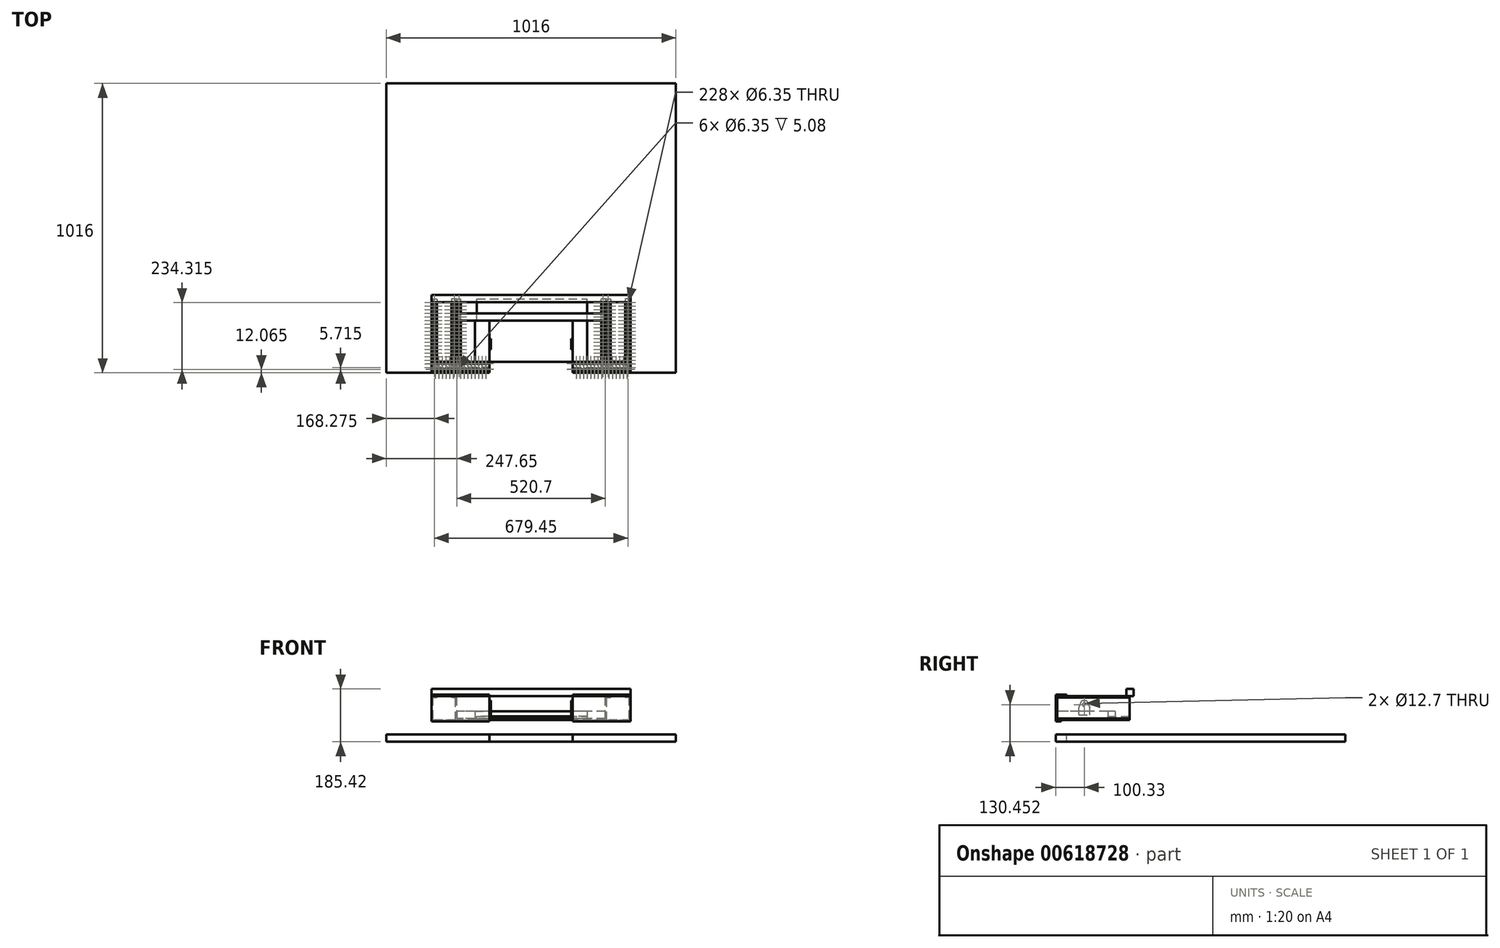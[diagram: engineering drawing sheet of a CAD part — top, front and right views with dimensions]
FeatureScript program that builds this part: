
annotation { "Feature Type Name" : "Feature", "Feature Type Description" : "" }
export const myFeature = defineFeature(function(context is Context, id is Id, definition is map)
    precondition{}
    {
        {
            var Q0;
            Q0=qCreatedBy(makeId("Top.planeOp"),FACE);
            var sketch = newSketch(context, id + "F0", { "sketchPlane" : qUnion([Q0])});
            skLineSegment(sketch, "E0.bottom", {"start": v(508, 508) * mm, "end": v(-508, 508) * mm});
            skLineSegment(sketch, "E0.top", {"start": v(508, -508) * mm, "end": v(-508, -508) * mm});
            skLineSegment(sketch, "E0.left", {"start": v(508, 508) * mm, "end": v(508, -508) * mm});
            skLineSegment(sketch, "E0.right", {"start": v(-508, 508) * mm, "end": v(-508, -508) * mm});
            skPoint(sketch, "E0.middle", {"position": v(0, 0) * mm});
            skSolve(sketch);
        }
        {
            var Q0;
            Q0=qSketchRegion(id+"F0",true);
            extrude(context, id + "F1", {"entities" : qUnion([Q0]), "depth" : 25.4 * mm, "offsetDistance" : 25.4 * mm});
        }
        {
            var Q0;
            Q0=makeQuery(id+"F1.opExtrude","SWEPT_FACE",FACE,{"disambiguationData":[OSD([sQuery(id+"F0.wireOp",EDGE,"E0.top")])]});
            var sketch = newSketch(context, id + "F2", { "sketchPlane" : qUnion([Q0])});
            skLineSegment(sketch, "E1.bottom", {"start": v(-349.25, 165.1) * mm, "end": v(349.25, 165.1) * mm});
            skLineSegment(sketch, "E1.top", {"start": v(-349.25, 76.2) * mm, "end": v(349.25, 76.2) * mm});
            skLineSegment(sketch, "E1.left", {"start": v(-349.25, 165.1) * mm, "end": v(-349.25, 76.2) * mm});
            skLineSegment(sketch, "E1.right", {"start": v(349.25, 165.1) * mm, "end": v(349.25, 76.2) * mm});
            skSolve(sketch);
        }
        {
            var Q0;
            Q0=qSketchRegion(id+"F2",true);
            extrude(context, id + "F3", {"entities" : qUnion([Q0]), "oppositeDirection" : true, "depth" : 5.08 * mm, "offsetDistance" : 25.4 * mm});
        }
        {
            var Q0;
            Q0=makeQuery(id+"F3.opExtrude","SWEPT_FACE",FACE,{"disambiguationData":[OSD([sQuery(id+"F2.wireOp",EDGE,"E1.bottom")])]});
            var sketch = newSketch(context, id + "F4", { "sketchPlane" : qUnion([Q0])});
            skLineSegment(sketch, "E2.bottom", {"start": v(-349.25, -469.9) * mm, "end": v(349.25, -469.9) * mm});
            skLineSegment(sketch, "E2.top", {"start": v(-349.25, -508) * mm, "end": v(349.25, -508) * mm});
            skLineSegment(sketch, "E2.left", {"start": v(-349.25, -469.9) * mm, "end": v(-349.25, -508) * mm});
            skLineSegment(sketch, "E2.right", {"start": v(349.25, -469.9) * mm, "end": v(349.25, -508) * mm});
            skCircle(sketch, "E3", {"center": v(-336.55, -476.25) * mm, "radius": 3.18 * mm});
            skCircle(sketch, "E4.0.1.0", {"center": v(-335.43, -495.27) * mm, "radius": 3.18 * mm});
            skCircle(sketch, "E4.1.0.0", {"center": v(-323.85, -476.25) * mm, "radius": 3.18 * mm});
            skCircle(sketch, "E4.1.1.0", {"center": v(-322.73, -495.27) * mm, "radius": 3.18 * mm});
            skCircle(sketch, "E4.2.0.0", {"center": v(-311.15, -476.25) * mm, "radius": 3.18 * mm});
            skCircle(sketch, "E4.2.1.0", {"center": v(-310.03, -495.27) * mm, "radius": 3.18 * mm});
            skCircle(sketch, "E4.3.0.0", {"center": v(-298.45, -476.25) * mm, "radius": 3.18 * mm});
            skCircle(sketch, "E4.3.1.0", {"center": v(-297.33, -495.27) * mm, "radius": 3.18 * mm});
            skCircle(sketch, "E4.4.0.0", {"center": v(-285.75, -476.25) * mm, "radius": 3.18 * mm});
            skCircle(sketch, "E4.4.1.0", {"center": v(-284.63, -495.27) * mm, "radius": 3.18 * mm});
            skCircle(sketch, "E4.5.0.0", {"center": v(-273.05, -476.25) * mm, "radius": 3.18 * mm});
            skCircle(sketch, "E4.5.1.0", {"center": v(-271.93, -495.27) * mm, "radius": 3.18 * mm});
            skCircle(sketch, "E4.6.0.0", {"center": v(-260.35, -476.25) * mm, "radius": 3.18 * mm});
            skCircle(sketch, "E4.6.1.0", {"center": v(-259.23, -495.27) * mm, "radius": 3.18 * mm});
            skCircle(sketch, "E4.7.0.0", {"center": v(-247.65, -476.25) * mm, "radius": 3.18 * mm});
            skCircle(sketch, "E4.7.1.0", {"center": v(-246.53, -495.27) * mm, "radius": 3.18 * mm});
            skCircle(sketch, "E4.8.0.0", {"center": v(-234.95, -476.25) * mm, "radius": 3.18 * mm});
            skCircle(sketch, "E4.8.1.0", {"center": v(-233.83, -495.27) * mm, "radius": 3.18 * mm});
            skCircle(sketch, "E4.9.0.0", {"center": v(-222.25, -476.25) * mm, "radius": 3.18 * mm});
            skCircle(sketch, "E4.9.1.0", {"center": v(-221.13, -495.27) * mm, "radius": 3.18 * mm});
            skCircle(sketch, "E4.10.0.0", {"center": v(-209.55, -476.25) * mm, "radius": 3.18 * mm});
            skCircle(sketch, "E4.10.1.0", {"center": v(-208.43, -495.27) * mm, "radius": 3.18 * mm});
            skCircle(sketch, "E4.11.0.0", {"center": v(-196.85, -476.25) * mm, "radius": 3.18 * mm});
            skCircle(sketch, "E4.11.1.0", {"center": v(-195.73, -495.27) * mm, "radius": 3.18 * mm});
            skCircle(sketch, "E4.12.0.0", {"center": v(-184.15, -476.25) * mm, "radius": 3.18 * mm});
            skCircle(sketch, "E4.12.1.0", {"center": v(-183.03, -495.27) * mm, "radius": 3.18 * mm});
            skCircle(sketch, "E4.13.0.0", {"center": v(-171.45, -476.25) * mm, "radius": 3.18 * mm});
            skCircle(sketch, "E4.13.1.0", {"center": v(-170.33, -495.27) * mm, "radius": 3.18 * mm});
            skCircle(sketch, "E4.14.0.0", {"center": v(-158.75, -476.25) * mm, "radius": 3.18 * mm});
            skCircle(sketch, "E4.14.1.0", {"center": v(-157.63, -495.27) * mm, "radius": 3.18 * mm});
            skCircle(sketch, "E4.15.0.0", {"center": v(-146.05, -476.25) * mm, "radius": 3.18 * mm});
            skCircle(sketch, "E4.15.1.0", {"center": v(-144.93, -495.27) * mm, "radius": 3.18 * mm});
            skCircle(sketch, "E4.16.0.0", {"center": v(-133.35, -476.25) * mm, "radius": 3.18 * mm});
            skCircle(sketch, "E4.16.1.0", {"center": v(-132.23, -495.27) * mm, "radius": 3.18 * mm});
            skCircle(sketch, "E4.17.0.0", {"center": v(-120.65, -476.25) * mm, "radius": 3.18 * mm});
            skCircle(sketch, "E4.17.1.0", {"center": v(-119.53, -495.27) * mm, "radius": 3.18 * mm});
            skCircle(sketch, "E4.18.0.0", {"center": v(-107.95, -476.25) * mm, "radius": 3.18 * mm});
            skCircle(sketch, "E4.18.1.0", {"center": v(-106.83, -495.27) * mm, "radius": 3.18 * mm});
            skCircle(sketch, "E4.19.0.0", {"center": v(-95.25, -476.25) * mm, "radius": 3.18 * mm});
            skCircle(sketch, "E4.19.1.0", {"center": v(-94.13, -495.27) * mm, "radius": 3.18 * mm});
            skCircle(sketch, "E4.20.0.0", {"center": v(-82.55, -476.25) * mm, "radius": 3.18 * mm});
            skCircle(sketch, "E4.20.1.0", {"center": v(-81.43, -495.27) * mm, "radius": 3.18 * mm});
            skCircle(sketch, "E4.21.0.0", {"center": v(-69.85, -476.25) * mm, "radius": 3.18 * mm});
            skCircle(sketch, "E4.21.1.0", {"center": v(-68.73, -495.27) * mm, "radius": 3.18 * mm});
            skCircle(sketch, "E4.22.0.0", {"center": v(-57.15, -476.25) * mm, "radius": 3.18 * mm});
            skCircle(sketch, "E4.22.1.0", {"center": v(-56.03, -495.27) * mm, "radius": 3.18 * mm});
            skCircle(sketch, "E4.23.0.0", {"center": v(-44.45, -476.25) * mm, "radius": 3.18 * mm});
            skCircle(sketch, "E4.23.1.0", {"center": v(-43.33, -495.27) * mm, "radius": 3.18 * mm});
            skCircle(sketch, "E4.24.0.0", {"center": v(-31.75, -476.25) * mm, "radius": 3.18 * mm});
            skCircle(sketch, "E4.24.1.0", {"center": v(-30.63, -495.27) * mm, "radius": 3.18 * mm});
            skCircle(sketch, "E4.25.0.0", {"center": v(-19.05, -476.25) * mm, "radius": 3.18 * mm});
            skCircle(sketch, "E4.25.1.0", {"center": v(-17.93, -495.27) * mm, "radius": 3.18 * mm});
            skCircle(sketch, "E4.26.0.0", {"center": v(-6.35, -476.25) * mm, "radius": 3.18 * mm});
            skCircle(sketch, "E4.26.1.0", {"center": v(-5.23, -495.27) * mm, "radius": 3.18 * mm});
            skCircle(sketch, "E4.27.0.0", {"center": v(6.35, -476.25) * mm, "radius": 3.18 * mm});
            skCircle(sketch, "E4.27.1.0", {"center": v(7.47, -495.27) * mm, "radius": 3.18 * mm});
            skCircle(sketch, "E4.28.0.0", {"center": v(19.05, -476.25) * mm, "radius": 3.18 * mm});
            skCircle(sketch, "E4.28.1.0", {"center": v(20.17, -495.27) * mm, "radius": 3.18 * mm});
            skCircle(sketch, "E4.29.0.0", {"center": v(31.75, -476.25) * mm, "radius": 3.18 * mm});
            skCircle(sketch, "E4.29.1.0", {"center": v(32.87, -495.27) * mm, "radius": 3.18 * mm});
            skCircle(sketch, "E4.30.0.0", {"center": v(44.45, -476.25) * mm, "radius": 3.18 * mm});
            skCircle(sketch, "E4.30.1.0", {"center": v(45.57, -495.27) * mm, "radius": 3.18 * mm});
            skCircle(sketch, "E4.31.0.0", {"center": v(57.15, -476.25) * mm, "radius": 3.18 * mm});
            skCircle(sketch, "E4.31.1.0", {"center": v(58.27, -495.27) * mm, "radius": 3.18 * mm});
            skCircle(sketch, "E4.32.0.0", {"center": v(69.85, -476.25) * mm, "radius": 3.18 * mm});
            skCircle(sketch, "E4.32.1.0", {"center": v(70.97, -495.27) * mm, "radius": 3.18 * mm});
            skCircle(sketch, "E4.33.0.0", {"center": v(82.55, -476.25) * mm, "radius": 3.18 * mm});
            skCircle(sketch, "E4.33.1.0", {"center": v(83.67, -495.27) * mm, "radius": 3.18 * mm});
            skCircle(sketch, "E4.34.0.0", {"center": v(95.25, -476.25) * mm, "radius": 3.18 * mm});
            skCircle(sketch, "E4.34.1.0", {"center": v(96.37, -495.27) * mm, "radius": 3.18 * mm});
            skCircle(sketch, "E4.35.0.0", {"center": v(107.95, -476.25) * mm, "radius": 3.18 * mm});
            skCircle(sketch, "E4.35.1.0", {"center": v(109.07, -495.27) * mm, "radius": 3.18 * mm});
            skCircle(sketch, "E4.36.0.0", {"center": v(120.65, -476.25) * mm, "radius": 3.18 * mm});
            skCircle(sketch, "E4.36.1.0", {"center": v(121.77, -495.27) * mm, "radius": 3.18 * mm});
            skCircle(sketch, "E4.37.0.0", {"center": v(133.35, -476.25) * mm, "radius": 3.18 * mm});
            skCircle(sketch, "E4.37.1.0", {"center": v(134.47, -495.27) * mm, "radius": 3.18 * mm});
            skCircle(sketch, "E4.38.0.0", {"center": v(146.05, -476.25) * mm, "radius": 3.18 * mm});
            skCircle(sketch, "E4.38.1.0", {"center": v(147.17, -495.27) * mm, "radius": 3.18 * mm});
            skCircle(sketch, "E4.39.0.0", {"center": v(158.75, -476.25) * mm, "radius": 3.18 * mm});
            skCircle(sketch, "E4.39.1.0", {"center": v(159.87, -495.27) * mm, "radius": 3.18 * mm});
            skCircle(sketch, "E4.40.0.0", {"center": v(171.45, -476.25) * mm, "radius": 3.18 * mm});
            skCircle(sketch, "E4.40.1.0", {"center": v(172.57, -495.27) * mm, "radius": 3.18 * mm});
            skCircle(sketch, "E4.41.0.0", {"center": v(184.15, -476.25) * mm, "radius": 3.18 * mm});
            skCircle(sketch, "E4.41.1.0", {"center": v(185.27, -495.27) * mm, "radius": 3.18 * mm});
            skCircle(sketch, "E4.42.0.0", {"center": v(196.85, -476.25) * mm, "radius": 3.18 * mm});
            skCircle(sketch, "E4.42.1.0", {"center": v(197.97, -495.27) * mm, "radius": 3.18 * mm});
            skCircle(sketch, "E4.43.0.0", {"center": v(209.55, -476.25) * mm, "radius": 3.18 * mm});
            skCircle(sketch, "E4.43.1.0", {"center": v(210.67, -495.27) * mm, "radius": 3.18 * mm});
            skCircle(sketch, "E4.44.0.0", {"center": v(222.25, -476.25) * mm, "radius": 3.18 * mm});
            skCircle(sketch, "E4.44.1.0", {"center": v(223.37, -495.27) * mm, "radius": 3.18 * mm});
            skCircle(sketch, "E4.45.0.0", {"center": v(234.95, -476.25) * mm, "radius": 3.18 * mm});
            skCircle(sketch, "E4.45.1.0", {"center": v(236.07, -495.27) * mm, "radius": 3.18 * mm});
            skCircle(sketch, "E4.46.0.0", {"center": v(247.65, -476.25) * mm, "radius": 3.18 * mm});
            skCircle(sketch, "E4.46.1.0", {"center": v(248.77, -495.27) * mm, "radius": 3.18 * mm});
            skCircle(sketch, "E4.47.0.0", {"center": v(260.35, -476.25) * mm, "radius": 3.18 * mm});
            skCircle(sketch, "E4.47.1.0", {"center": v(261.47, -495.27) * mm, "radius": 3.18 * mm});
            skCircle(sketch, "E4.48.0.0", {"center": v(273.05, -476.25) * mm, "radius": 3.18 * mm});
            skCircle(sketch, "E4.48.1.0", {"center": v(274.17, -495.27) * mm, "radius": 3.18 * mm});
            skCircle(sketch, "E4.49.0.0", {"center": v(285.75, -476.25) * mm, "radius": 3.18 * mm});
            skCircle(sketch, "E4.49.1.0", {"center": v(286.87, -495.27) * mm, "radius": 3.18 * mm});
            skCircle(sketch, "E4.50.0.0", {"center": v(298.45, -476.25) * mm, "radius": 3.18 * mm});
            skCircle(sketch, "E4.50.1.0", {"center": v(299.57, -495.27) * mm, "radius": 3.18 * mm});
            skCircle(sketch, "E4.51.0.0", {"center": v(311.15, -476.25) * mm, "radius": 3.18 * mm});
            skCircle(sketch, "E4.51.1.0", {"center": v(312.27, -495.27) * mm, "radius": 3.18 * mm});
            skCircle(sketch, "E4.52.0.0", {"center": v(323.85, -476.25) * mm, "radius": 3.18 * mm});
            skCircle(sketch, "E4.52.1.0", {"center": v(324.97, -495.27) * mm, "radius": 3.18 * mm});
            skCircle(sketch, "E4.53.0.0", {"center": v(336.55, -476.25) * mm, "radius": 3.18 * mm});
            skCircle(sketch, "E4.53.1.0", {"center": v(337.67, -495.27) * mm, "radius": 3.18 * mm});
            skLineSegment(sketch, "E4.direction1", {"start": v(-336.55, -476.25) * mm, "end": v(-323.85, -476.25) * mm, "construction": true});
            skLineSegment(sketch, "E4.direction2", {"start": v(-336.55, -476.25) * mm, "end": v(-335.43, -495.27) * mm, "construction": true});
            skSolve(sketch);
        }
        {
            var Q0;
            Q0=qSketchRegion(id+"F4",true);
            extrude(context, id + "F5", {"entities" : qUnion([Q0]), "oppositeDirection" : true, "depth" : 5.08 * mm, "offsetDistance" : 25.4 * mm});
        }
        {
            var Q0;
            Q0=makeQuery(id+"F3.opExtrude","SWEPT_FACE",FACE,{"disambiguationData":[OSD([sQuery(id+"F2.wireOp",EDGE,"E1.top")])]});
            var sketch = newSketch(context, id + "F6", { "sketchPlane" : qUnion([Q0])});
            skLineSegment(sketch, "E5.bottom", {"start": v(-349.25, 508) * mm, "end": v(349.25, 508) * mm});
            skLineSegment(sketch, "E5.top", {"start": v(-349.25, 488.95) * mm, "end": v(349.25, 488.95) * mm});
            skLineSegment(sketch, "E5.left", {"start": v(-349.25, 508) * mm, "end": v(-349.25, 488.95) * mm});
            skLineSegment(sketch, "E5.right", {"start": v(349.25, 508) * mm, "end": v(349.25, 488.95) * mm});
            skCircle(sketch, "E6", {"center": v(-336.55, 495.94) * mm, "radius": 3.18 * mm});
            skCircle(sketch, "E7.1.0.0", {"center": v(-323.85, 495.94) * mm, "radius": 3.18 * mm});
            skCircle(sketch, "E7.2.0.0", {"center": v(-311.15, 495.94) * mm, "radius": 3.18 * mm});
            skCircle(sketch, "E7.3.0.0", {"center": v(-298.45, 495.94) * mm, "radius": 3.18 * mm});
            skCircle(sketch, "E7.4.0.0", {"center": v(-285.75, 495.94) * mm, "radius": 3.18 * mm});
            skCircle(sketch, "E7.5.0.0", {"center": v(-273.05, 495.94) * mm, "radius": 3.18 * mm});
            skCircle(sketch, "E7.6.0.0", {"center": v(-260.35, 495.94) * mm, "radius": 3.18 * mm});
            skCircle(sketch, "E7.7.0.0", {"center": v(-247.65, 495.94) * mm, "radius": 3.18 * mm});
            skCircle(sketch, "E7.8.0.0", {"center": v(-234.95, 495.94) * mm, "radius": 3.18 * mm});
            skCircle(sketch, "E7.9.0.0", {"center": v(-222.25, 495.94) * mm, "radius": 3.18 * mm});
            skCircle(sketch, "E7.10.0.0", {"center": v(-209.55, 495.94) * mm, "radius": 3.18 * mm});
            skCircle(sketch, "E7.11.0.0", {"center": v(-196.85, 495.94) * mm, "radius": 3.18 * mm});
            skCircle(sketch, "E7.12.0.0", {"center": v(-184.15, 495.94) * mm, "radius": 3.18 * mm});
            skCircle(sketch, "E7.13.0.0", {"center": v(-171.45, 495.94) * mm, "radius": 3.18 * mm});
            skCircle(sketch, "E7.14.0.0", {"center": v(-158.75, 495.94) * mm, "radius": 3.18 * mm});
            skCircle(sketch, "E7.15.0.0", {"center": v(-146.05, 495.94) * mm, "radius": 3.18 * mm});
            skCircle(sketch, "E7.16.0.0", {"center": v(-133.35, 495.94) * mm, "radius": 3.18 * mm});
            skCircle(sketch, "E7.17.0.0", {"center": v(-120.65, 495.94) * mm, "radius": 3.18 * mm});
            skCircle(sketch, "E7.18.0.0", {"center": v(-107.95, 495.94) * mm, "radius": 3.18 * mm});
            skCircle(sketch, "E7.19.0.0", {"center": v(-95.25, 495.94) * mm, "radius": 3.18 * mm});
            skCircle(sketch, "E7.20.0.0", {"center": v(-82.55, 495.94) * mm, "radius": 3.18 * mm});
            skCircle(sketch, "E7.21.0.0", {"center": v(-69.85, 495.94) * mm, "radius": 3.18 * mm});
            skCircle(sketch, "E7.22.0.0", {"center": v(-57.15, 495.94) * mm, "radius": 3.18 * mm});
            skCircle(sketch, "E7.23.0.0", {"center": v(-44.45, 495.94) * mm, "radius": 3.18 * mm});
            skCircle(sketch, "E7.24.0.0", {"center": v(-31.75, 495.94) * mm, "radius": 3.18 * mm});
            skCircle(sketch, "E7.25.0.0", {"center": v(-19.05, 495.94) * mm, "radius": 3.18 * mm});
            skCircle(sketch, "E7.26.0.0", {"center": v(-6.35, 495.94) * mm, "radius": 3.18 * mm});
            skCircle(sketch, "E7.27.0.0", {"center": v(6.35, 495.94) * mm, "radius": 3.18 * mm});
            skCircle(sketch, "E7.28.0.0", {"center": v(19.05, 495.94) * mm, "radius": 3.18 * mm});
            skCircle(sketch, "E7.29.0.0", {"center": v(31.75, 495.94) * mm, "radius": 3.18 * mm});
            skCircle(sketch, "E7.30.0.0", {"center": v(44.45, 495.94) * mm, "radius": 3.18 * mm});
            skCircle(sketch, "E7.31.0.0", {"center": v(57.15, 495.94) * mm, "radius": 3.18 * mm});
            skCircle(sketch, "E7.32.0.0", {"center": v(69.85, 495.94) * mm, "radius": 3.18 * mm});
            skCircle(sketch, "E7.33.0.0", {"center": v(82.55, 495.94) * mm, "radius": 3.18 * mm});
            skCircle(sketch, "E7.34.0.0", {"center": v(95.25, 495.94) * mm, "radius": 3.18 * mm});
            skCircle(sketch, "E7.35.0.0", {"center": v(107.95, 495.94) * mm, "radius": 3.18 * mm});
            skCircle(sketch, "E7.36.0.0", {"center": v(120.65, 495.94) * mm, "radius": 3.18 * mm});
            skCircle(sketch, "E7.37.0.0", {"center": v(133.35, 495.94) * mm, "radius": 3.18 * mm});
            skCircle(sketch, "E7.38.0.0", {"center": v(146.05, 495.94) * mm, "radius": 3.18 * mm});
            skCircle(sketch, "E7.39.0.0", {"center": v(158.75, 495.94) * mm, "radius": 3.18 * mm});
            skCircle(sketch, "E7.40.0.0", {"center": v(171.45, 495.94) * mm, "radius": 3.18 * mm});
            skCircle(sketch, "E7.41.0.0", {"center": v(184.15, 495.94) * mm, "radius": 3.18 * mm});
            skCircle(sketch, "E7.42.0.0", {"center": v(196.85, 495.94) * mm, "radius": 3.18 * mm});
            skCircle(sketch, "E7.43.0.0", {"center": v(209.55, 495.94) * mm, "radius": 3.18 * mm});
            skCircle(sketch, "E7.44.0.0", {"center": v(222.25, 495.94) * mm, "radius": 3.18 * mm});
            skCircle(sketch, "E7.45.0.0", {"center": v(234.95, 495.94) * mm, "radius": 3.18 * mm});
            skCircle(sketch, "E7.46.0.0", {"center": v(247.65, 495.94) * mm, "radius": 3.18 * mm});
            skCircle(sketch, "E7.47.0.0", {"center": v(260.35, 495.94) * mm, "radius": 3.18 * mm});
            skCircle(sketch, "E7.48.0.0", {"center": v(273.05, 495.94) * mm, "radius": 3.18 * mm});
            skCircle(sketch, "E7.49.0.0", {"center": v(285.75, 495.94) * mm, "radius": 3.18 * mm});
            skCircle(sketch, "E7.50.0.0", {"center": v(298.45, 495.94) * mm, "radius": 3.18 * mm});
            skCircle(sketch, "E7.51.0.0", {"center": v(311.15, 495.94) * mm, "radius": 3.18 * mm});
            skCircle(sketch, "E7.52.0.0", {"center": v(323.85, 495.94) * mm, "radius": 3.18 * mm});
            skCircle(sketch, "E7.53.0.0", {"center": v(336.55, 495.94) * mm, "radius": 3.18 * mm});
            skLineSegment(sketch, "E7.direction1", {"start": v(-336.55, 495.94) * mm, "end": v(-323.85, 495.94) * mm, "construction": true});
            skSolve(sketch);
        }
        {
            var Q0;
            Q0=qSketchRegion(id+"F6",true);
            extrude(context, id + "F7", {"entities" : qUnion([Q0]), "operationType" : NewBodyOperationType.ADD, "depth" : 5.08 * mm, "offsetDistance" : 25.4 * mm});
        }
        {
            var Q0;
            Q0=makeQuery(id+"F3.opExtrude","CAP_FACE",FACE,{"disambiguationData":[OSD([sQuery(id+"F2.wireOp",EDGE,"E1.bottom"),sQuery(id+"F2.wireOp",EDGE,"E1.top"),sQuery(id+"F2.wireOp",EDGE,"E1.left"),sQuery(id+"F2.wireOp",EDGE,"E1.right")])],"isStart":false});
            var sketch = newSketch(context, id + "F8", { "sketchPlane" : qUnion([Q0])});
            skLineSegment(sketch, "E8.top", {"start": v(-349.25, 154.94) * mm, "end": v(-344.17, 154.94) * mm});
            skLineSegment(sketch, "E8.left", {"start": v(-349.25, 81.28) * mm, "end": v(-349.25, 154.94) * mm});
            skLineSegment(sketch, "E8.right", {"start": v(-344.17, 81.28) * mm, "end": v(-344.17, 154.94) * mm});
            skLineSegment(sketch, "E9.top", {"start": v(-265.43, 154.94) * mm, "end": v(-260.35, 154.94) * mm});
            skLineSegment(sketch, "E9.left", {"start": v(-265.43, 81.28) * mm, "end": v(-265.43, 154.94) * mm});
            skLineSegment(sketch, "E9.right", {"start": v(-260.35, 81.28) * mm, "end": v(-260.35, 154.94) * mm});
            skLineSegment(sketch, "E10", {"start": v(-265.43, 81.28) * mm, "end": v(-260.35, 81.28) * mm});
            skLineSegment(sketch, "E11", {"start": v(-349.25, 81.28) * mm, "end": v(-344.17, 81.28) * mm});
            skSolve(sketch);
        }
        {
            var Q0;
            Q0=qSketchRegion(id+"F8",true);
            extrude(context, id + "F9", {"entities" : qUnion([Q0]), "operationType" : NewBodyOperationType.ADD, "depth" : 254 * mm, "offsetDistance" : 25.4 * mm});
        }
        {
            var Q0;
            Q0=makeQuery(id+"F9.opExtrude","SWEPT_FACE",FACE,{"disambiguationData":[OSD([sQuery(id+"F8.wireOp",EDGE,"E8.top")])]});
            var sketch = newSketch(context, id + "F10", { "sketchPlane" : qUnion([Q0])});
            skLineSegment(sketch, "E12.bottom", {"start": v(349.25, -248.92) * mm, "end": v(330.2, -248.92) * mm});
            skLineSegment(sketch, "E12.top", {"start": v(349.25, -502.92) * mm, "end": v(330.2, -502.92) * mm});
            skLineSegment(sketch, "E12.left", {"start": v(349.25, -248.92) * mm, "end": v(349.25, -502.92) * mm});
            skLineSegment(sketch, "E12.right", {"start": v(330.2, -248.92) * mm, "end": v(330.2, -502.92) * mm});
            skLineSegment(sketch, "E13.bottom", {"start": v(260.35, -248.92) * mm, "end": v(279.4, -248.92) * mm});
            skLineSegment(sketch, "E13.top", {"start": v(260.35, -502.92) * mm, "end": v(279.4, -502.92) * mm});
            skLineSegment(sketch, "E13.left", {"start": v(260.35, -248.92) * mm, "end": v(260.35, -502.92) * mm});
            skLineSegment(sketch, "E13.right", {"start": v(279.4, -248.92) * mm, "end": v(279.4, -502.92) * mm});
            skCircle(sketch, "E14", {"center": v(269.88, -261.62) * mm, "radius": 3.18 * mm});
            skCircle(sketch, "E15.0.1.0", {"center": v(269.88, -274.32) * mm, "radius": 3.18 * mm});
            skCircle(sketch, "E15.0.2.0", {"center": v(269.88, -287.02) * mm, "radius": 3.18 * mm});
            skCircle(sketch, "E15.0.3.0", {"center": v(269.88, -299.72) * mm, "radius": 3.18 * mm});
            skCircle(sketch, "E15.0.4.0", {"center": v(269.88, -312.42) * mm, "radius": 3.18 * mm});
            skCircle(sketch, "E15.0.5.0", {"center": v(269.88, -325.12) * mm, "radius": 3.18 * mm});
            skCircle(sketch, "E15.0.6.0", {"center": v(269.88, -337.82) * mm, "radius": 3.18 * mm});
            skCircle(sketch, "E15.0.7.0", {"center": v(269.88, -350.52) * mm, "radius": 3.18 * mm});
            skCircle(sketch, "E15.0.8.0", {"center": v(269.88, -363.22) * mm, "radius": 3.18 * mm});
            skCircle(sketch, "E15.0.9.0", {"center": v(269.88, -375.92) * mm, "radius": 3.18 * mm});
            skCircle(sketch, "E15.0.10.0", {"center": v(269.88, -388.62) * mm, "radius": 3.18 * mm});
            skCircle(sketch, "E15.0.11.0", {"center": v(269.88, -401.32) * mm, "radius": 3.18 * mm});
            skCircle(sketch, "E15.0.12.0", {"center": v(269.88, -414.02) * mm, "radius": 3.18 * mm});
            skCircle(sketch, "E15.0.13.0", {"center": v(269.88, -426.72) * mm, "radius": 3.18 * mm});
            skCircle(sketch, "E15.0.14.0", {"center": v(269.88, -439.42) * mm, "radius": 3.18 * mm});
            skCircle(sketch, "E15.0.15.0", {"center": v(269.88, -452.12) * mm, "radius": 3.18 * mm});
            skCircle(sketch, "E15.0.16.0", {"center": v(269.88, -464.82) * mm, "radius": 3.18 * mm});
            skCircle(sketch, "E15.0.17.0", {"center": v(269.88, -477.52) * mm, "radius": 3.18 * mm});
            skCircle(sketch, "E15.0.18.0", {"center": v(269.88, -490.22) * mm, "radius": 3.18 * mm});
            skCircle(sketch, "E15.1.0.0", {"center": v(339.73, -261.62) * mm, "radius": 3.18 * mm});
            skCircle(sketch, "E15.1.1.0", {"center": v(339.73, -274.32) * mm, "radius": 3.18 * mm});
            skCircle(sketch, "E15.1.2.0", {"center": v(339.73, -287.02) * mm, "radius": 3.18 * mm});
            skCircle(sketch, "E15.1.3.0", {"center": v(339.73, -299.72) * mm, "radius": 3.18 * mm});
            skCircle(sketch, "E15.1.4.0", {"center": v(339.73, -312.42) * mm, "radius": 3.18 * mm});
            skCircle(sketch, "E15.1.5.0", {"center": v(339.73, -325.12) * mm, "radius": 3.18 * mm});
            skCircle(sketch, "E15.1.6.0", {"center": v(339.73, -337.82) * mm, "radius": 3.18 * mm});
            skCircle(sketch, "E15.1.7.0", {"center": v(339.73, -350.52) * mm, "radius": 3.18 * mm});
            skCircle(sketch, "E15.1.8.0", {"center": v(339.73, -363.22) * mm, "radius": 3.18 * mm});
            skCircle(sketch, "E15.1.9.0", {"center": v(339.73, -375.92) * mm, "radius": 3.18 * mm});
            skCircle(sketch, "E15.1.10.0", {"center": v(339.73, -388.62) * mm, "radius": 3.18 * mm});
            skCircle(sketch, "E15.1.11.0", {"center": v(339.73, -401.32) * mm, "radius": 3.18 * mm});
            skCircle(sketch, "E15.1.12.0", {"center": v(339.73, -414.02) * mm, "radius": 3.18 * mm});
            skCircle(sketch, "E15.1.13.0", {"center": v(339.73, -426.72) * mm, "radius": 3.18 * mm});
            skCircle(sketch, "E15.1.14.0", {"center": v(339.73, -439.42) * mm, "radius": 3.18 * mm});
            skCircle(sketch, "E15.1.15.0", {"center": v(339.73, -452.12) * mm, "radius": 3.18 * mm});
            skCircle(sketch, "E15.1.16.0", {"center": v(339.73, -464.82) * mm, "radius": 3.18 * mm});
            skCircle(sketch, "E15.1.17.0", {"center": v(339.73, -477.52) * mm, "radius": 3.18 * mm});
            skCircle(sketch, "E15.1.18.0", {"center": v(339.73, -490.22) * mm, "radius": 3.18 * mm});
            skLineSegment(sketch, "E15.direction1", {"start": v(269.88, -261.62) * mm, "end": v(339.73, -261.62) * mm, "construction": true});
            skLineSegment(sketch, "E15.direction2", {"start": v(269.88, -261.62) * mm, "end": v(269.88, -274.32) * mm, "construction": true});
            skSolve(sketch);
        }
        {
            var Q0;
            Q0=qSketchRegion(id+"F10",true);
            extrude(context, id + "F11", {"entities" : qUnion([Q0]), "depth" : 5.08 * mm, "offsetDistance" : 25.4 * mm});
        }
        {
            var Q0;
            Q0=makeQuery(id+"F9.opExtrude","SWEPT_FACE",FACE,{"disambiguationData":[OSD([sQuery(id+"F8.wireOp",EDGE,"E10")])]});
            var sketch = newSketch(context, id + "F12", { "sketchPlane" : qUnion([Q0])});
            skLineSegment(sketch, "E16.bottom", {"start": v(246.38, 502.92) * mm, "end": v(265.43, 502.92) * mm});
            skLineSegment(sketch, "E16.top", {"start": v(246.38, 248.92) * mm, "end": v(265.43, 248.92) * mm});
            skLineSegment(sketch, "E16.left", {"start": v(246.38, 502.92) * mm, "end": v(246.38, 248.92) * mm});
            skLineSegment(sketch, "E16.right", {"start": v(265.43, 502.92) * mm, "end": v(265.43, 248.92) * mm});
            skCircle(sketch, "E17", {"center": v(252.73, 261.62) * mm, "radius": 3.18 * mm});
            skCircle(sketch, "E18.0.1.0", {"center": v(252.73, 274.32) * mm, "radius": 3.18 * mm});
            skCircle(sketch, "E18.0.2.0", {"center": v(252.73, 287.02) * mm, "radius": 3.18 * mm});
            skCircle(sketch, "E18.0.3.0", {"center": v(252.73, 299.72) * mm, "radius": 3.18 * mm});
            skCircle(sketch, "E18.0.4.0", {"center": v(252.73, 312.42) * mm, "radius": 3.18 * mm});
            skCircle(sketch, "E18.0.5.0", {"center": v(252.73, 325.12) * mm, "radius": 3.18 * mm});
            skCircle(sketch, "E18.0.6.0", {"center": v(252.73, 337.82) * mm, "radius": 3.18 * mm});
            skCircle(sketch, "E18.0.7.0", {"center": v(252.73, 350.52) * mm, "radius": 3.18 * mm});
            skCircle(sketch, "E18.0.8.0", {"center": v(252.73, 363.22) * mm, "radius": 3.18 * mm});
            skCircle(sketch, "E18.0.9.0", {"center": v(252.73, 375.92) * mm, "radius": 3.18 * mm});
            skCircle(sketch, "E18.0.10.0", {"center": v(252.73, 388.62) * mm, "radius": 3.18 * mm});
            skCircle(sketch, "E18.0.11.0", {"center": v(252.73, 401.32) * mm, "radius": 3.18 * mm});
            skCircle(sketch, "E18.0.12.0", {"center": v(252.73, 414.02) * mm, "radius": 3.18 * mm});
            skCircle(sketch, "E18.0.13.0", {"center": v(252.73, 426.72) * mm, "radius": 3.18 * mm});
            skCircle(sketch, "E18.0.14.0", {"center": v(252.73, 439.42) * mm, "radius": 3.18 * mm});
            skCircle(sketch, "E18.0.15.0", {"center": v(252.73, 452.12) * mm, "radius": 3.18 * mm});
            skCircle(sketch, "E18.0.16.0", {"center": v(252.73, 464.82) * mm, "radius": 3.18 * mm});
            skCircle(sketch, "E18.0.17.0", {"center": v(252.73, 477.52) * mm, "radius": 3.18 * mm});
            skCircle(sketch, "E18.0.18.0", {"center": v(252.73, 490.22) * mm, "radius": 3.18 * mm});
            skLineSegment(sketch, "E18.direction1", {"start": v(252.73, 261.62) * mm, "end": v(278.13, 261.62) * mm, "construction": true});
            skLineSegment(sketch, "E18.direction2", {"start": v(252.73, 261.62) * mm, "end": v(252.73, 274.32) * mm, "construction": true});
            skSolve(sketch);
        }
        {
            var Q0;
            Q0=qSketchRegion(id+"F12",true);
            extrude(context, id + "F13", {"entities" : qUnion([Q0]), "operationType" : NewBodyOperationType.ADD, "depth" : 5.08 * mm, "offsetDistance" : 25.4 * mm});
        }
        {
            var Q0;
            Q0=makeQuery(id+"F3.opExtrude","SWEPT_BODY",BODY,{"disambiguationData":[OSD([sQuery(id+"F2.wireOp",EDGE,"E1.bottom"),sQuery(id+"F2.wireOp",EDGE,"E1.top"),sQuery(id+"F2.wireOp",EDGE,"E1.left"),sQuery(id+"F2.wireOp",EDGE,"E1.right")])]});
            var Q1;
            Q1=makeQuery(id+"F11.opExtrude","SWEPT_BODY",BODY,{"disambiguationData":[OSD([sQuery(id+"F10.wireOp",EDGE,"E13.bottom"),sQuery(id+"F10.wireOp",EDGE,"E13.top"),sQuery(id+"F10.wireOp",EDGE,"E13.left"),sQuery(id+"F10.wireOp",EDGE,"E13.right"),sQuery(id+"F10.wireOp",EDGE,"E14"),sQuery(id+"F10.wireOp",EDGE,"E15.0.1.0"),sQuery(id+"F10.wireOp",EDGE,"E15.0.2.0"),sQuery(id+"F10.wireOp",EDGE,"E15.0.3.0"),sQuery(id+"F10.wireOp",EDGE,"E15.0.4.0"),sQuery(id+"F10.wireOp",EDGE,"E15.0.5.0"),sQuery(id+"F10.wireOp",EDGE,"E15.0.6.0"),sQuery(id+"F10.wireOp",EDGE,"E15.0.7.0"),sQuery(id+"F10.wireOp",EDGE,"E15.0.8.0"),sQuery(id+"F10.wireOp",EDGE,"E15.0.9.0"),sQuery(id+"F10.wireOp",EDGE,"E15.0.10.0"),sQuery(id+"F10.wireOp",EDGE,"E15.0.11.0"),sQuery(id+"F10.wireOp",EDGE,"E15.0.12.0"),sQuery(id+"F10.wireOp",EDGE,"E15.0.13.0"),sQuery(id+"F10.wireOp",EDGE,"E15.0.14.0"),sQuery(id+"F10.wireOp",EDGE,"E15.0.15.0"),sQuery(id+"F10.wireOp",EDGE,"E15.0.16.0"),sQuery(id+"F10.wireOp",EDGE,"E15.0.17.0"),sQuery(id+"F10.wireOp",EDGE,"E15.0.18.0")])]});
            var Q2;
            Q2=makeQuery(id+"F11.opExtrude","SWEPT_BODY",BODY,{"disambiguationData":[OSD([sQuery(id+"F10.wireOp",EDGE,"E12.bottom"),sQuery(id+"F10.wireOp",EDGE,"E12.top"),sQuery(id+"F10.wireOp",EDGE,"E12.left"),sQuery(id+"F10.wireOp",EDGE,"E12.right"),sQuery(id+"F10.wireOp",EDGE,"E15.1.0.0"),sQuery(id+"F10.wireOp",EDGE,"E15.1.1.0"),sQuery(id+"F10.wireOp",EDGE,"E15.1.2.0"),sQuery(id+"F10.wireOp",EDGE,"E15.1.3.0"),sQuery(id+"F10.wireOp",EDGE,"E15.1.4.0"),sQuery(id+"F10.wireOp",EDGE,"E15.1.5.0"),sQuery(id+"F10.wireOp",EDGE,"E15.1.6.0"),sQuery(id+"F10.wireOp",EDGE,"E15.1.7.0"),sQuery(id+"F10.wireOp",EDGE,"E15.1.8.0"),sQuery(id+"F10.wireOp",EDGE,"E15.1.9.0"),sQuery(id+"F10.wireOp",EDGE,"E15.1.10.0"),sQuery(id+"F10.wireOp",EDGE,"E15.1.11.0"),sQuery(id+"F10.wireOp",EDGE,"E15.1.12.0"),sQuery(id+"F10.wireOp",EDGE,"E15.1.13.0"),sQuery(id+"F10.wireOp",EDGE,"E15.1.14.0"),sQuery(id+"F10.wireOp",EDGE,"E15.1.15.0"),sQuery(id+"F10.wireOp",EDGE,"E15.1.16.0"),sQuery(id+"F10.wireOp",EDGE,"E15.1.17.0"),sQuery(id+"F10.wireOp",EDGE,"E15.1.18.0")])]});
            var Q3;
            Q3=qCreatedBy(makeId("Right.planeOp"),FACE);
            mirror(context, id + "F14", {"entities" : qUnion([Q0, Q1, Q2]), "mirrorPlane" : qUnion([Q3])});
        }
        {
            var Q0;
            Q0=makeQuery(id+"F14.opPattern","COPY",FACE,{"derivedFrom":makeQuery(id+"F11.opExtrude","CAP_FACE",FACE,{"disambiguationData":[OSD([sQuery(id+"F10.wireOp",EDGE,"E12.bottom"),sQuery(id+"F10.wireOp",EDGE,"E12.top"),sQuery(id+"F10.wireOp",EDGE,"E12.left"),sQuery(id+"F10.wireOp",EDGE,"E12.right"),sQuery(id+"F10.wireOp",EDGE,"E15.1.0.0"),sQuery(id+"F10.wireOp",EDGE,"E15.1.1.0"),sQuery(id+"F10.wireOp",EDGE,"E15.1.2.0"),sQuery(id+"F10.wireOp",EDGE,"E15.1.3.0"),sQuery(id+"F10.wireOp",EDGE,"E15.1.4.0"),sQuery(id+"F10.wireOp",EDGE,"E15.1.5.0"),sQuery(id+"F10.wireOp",EDGE,"E15.1.6.0"),sQuery(id+"F10.wireOp",EDGE,"E15.1.7.0"),sQuery(id+"F10.wireOp",EDGE,"E15.1.8.0"),sQuery(id+"F10.wireOp",EDGE,"E15.1.9.0"),sQuery(id+"F10.wireOp",EDGE,"E15.1.10.0"),sQuery(id+"F10.wireOp",EDGE,"E15.1.11.0"),sQuery(id+"F10.wireOp",EDGE,"E15.1.12.0"),sQuery(id+"F10.wireOp",EDGE,"E15.1.13.0"),sQuery(id+"F10.wireOp",EDGE,"E15.1.14.0"),sQuery(id+"F10.wireOp",EDGE,"E15.1.15.0"),sQuery(id+"F10.wireOp",EDGE,"E15.1.16.0"),sQuery(id+"F10.wireOp",EDGE,"E15.1.17.0"),sQuery(id+"F10.wireOp",EDGE,"E15.1.18.0")])],"isStart":false}),"instanceName":"1"});
            var sketch = newSketch(context, id + "F15", { "sketchPlane" : qUnion([Q0])});
            skLineSegment(sketch, "E19.bottom", {"start": v(-349.25, -234.95) * mm, "end": v(349.25, -234.95) * mm});
            skLineSegment(sketch, "E19.top", {"start": v(-349.25, -260.35) * mm, "end": v(349.25, -260.35) * mm});
            skLineSegment(sketch, "E19.left", {"start": v(-349.25, -234.95) * mm, "end": v(-349.25, -260.35) * mm});
            skLineSegment(sketch, "E19.right", {"start": v(349.25, -234.95) * mm, "end": v(349.25, -260.35) * mm});
            skSolve(sketch);
        }
        {
            var Q0;
            Q0=qSketchRegion(id+"F15",true);
            extrude(context, id + "F16", {"entities" : qUnion([Q0]), "depth" : 25.4 * mm, "offsetDistance" : 25.4 * mm});
        }
        {
            var Q0;
            {var subQ0=sQuery(id+"F6.wireOp",EDGE,"E7.41.0.0");var subQ1=sQuery(id+"F6.wireOp",EDGE,"E7.40.0.0");var subQ2=sQuery(id+"F6.wireOp",EDGE,"E7.39.0.0");var subQ3=sQuery(id+"F6.wireOp",EDGE,"E7.38.0.0");var subQ4=sQuery(id+"F6.wireOp",EDGE,"E7.37.0.0");var subQ5=sQuery(id+"F6.wireOp",EDGE,"E7.35.0.0");var subQ6=sQuery(id+"F6.wireOp",EDGE,"E7.33.0.0");var subQ7=sQuery(id+"F6.wireOp",EDGE,"E7.32.0.0");var subQ8=sQuery(id+"F6.wireOp",EDGE,"E7.31.0.0");var subQ9=sQuery(id+"F6.wireOp",EDGE,"E7.30.0.0");var subQ10=sQuery(id+"F6.wireOp",EDGE,"E7.29.0.0");var subQ11=sQuery(id+"F6.wireOp",EDGE,"E7.28.0.0");var subQ12=sQuery(id+"F6.wireOp",EDGE,"E7.27.0.0");var subQ13=sQuery(id+"F6.wireOp",EDGE,"E7.26.0.0");var subQ14=sQuery(id+"F6.wireOp",EDGE,"E7.25.0.0");var subQ15=sQuery(id+"F6.wireOp",EDGE,"E7.24.0.0");var subQ16=sQuery(id+"F6.wireOp",EDGE,"E7.23.0.0");var subQ17=sQuery(id+"F6.wireOp",EDGE,"E7.22.0.0");var subQ18=sQuery(id+"F6.wireOp",EDGE,"E7.21.0.0");var subQ19=sQuery(id+"F6.wireOp",EDGE,"E7.20.0.0");var subQ20=sQuery(id+"F6.wireOp",EDGE,"E7.19.0.0");var subQ21=sQuery(id+"F6.wireOp",EDGE,"E7.18.0.0");var subQ22=sQuery(id+"F6.wireOp",EDGE,"E7.4.0.0");var subQ23=sQuery(id+"F6.wireOp",EDGE,"E7.3.0.0");var subQ24=sQuery(id+"F6.wireOp",EDGE,"E7.2.0.0");var subQ25=sQuery(id+"F6.wireOp",EDGE,"E7.1.0.0");var subQ26=sQuery(id+"F6.wireOp",EDGE,"E6");var subQ27=sQuery(id+"F6.wireOp",EDGE,"E7.5.0.0");var subQ28=sQuery(id+"F6.wireOp",EDGE,"E7.34.0.0");var subQ29=sQuery(id+"F2.wireOp",EDGE,"E1.left");var subQ30=sQuery(id+"F6.wireOp",EDGE,"E7.11.0.0");var subQ31=sQuery(id+"F6.wireOp",EDGE,"E7.36.0.0");var subQ32=sQuery(id+"F6.wireOp",EDGE,"E7.13.0.0");var subQ33=sQuery(id+"F6.wireOp",EDGE,"E5.top");var subQ34=sQuery(id+"F6.wireOp",EDGE,"E5.left");var subQ35=sQuery(id+"F6.wireOp",EDGE,"E7.6.0.0");var subQ36=sQuery(id+"F6.wireOp",EDGE,"E7.7.0.0");var subQ37=sQuery(id+"F6.wireOp",EDGE,"E7.8.0.0");var subQ38=sQuery(id+"F6.wireOp",EDGE,"E7.9.0.0");var subQ39=sQuery(id+"F6.wireOp",EDGE,"E7.10.0.0");var subQ40=sQuery(id+"F6.wireOp",EDGE,"E7.12.0.0");var subQ41=sQuery(id+"F6.wireOp",EDGE,"E7.14.0.0");var subQ42=sQuery(id+"F6.wireOp",EDGE,"E7.15.0.0");var subQ43=sQuery(id+"F6.wireOp",EDGE,"E7.16.0.0");var subQ44=sQuery(id+"F6.wireOp",EDGE,"E7.17.0.0");var subQ45=sQuery(id+"F6.wireOp",EDGE,"E7.42.0.0");var subQ46=sQuery(id+"F6.wireOp",EDGE,"E7.43.0.0");var subQ47=sQuery(id+"F6.wireOp",EDGE,"E7.44.0.0");var subQ48=sQuery(id+"F6.wireOp",EDGE,"E7.45.0.0");var subQ49=sQuery(id+"F6.wireOp",EDGE,"E7.46.0.0");Q0=makeQuery(id+"F13.boolean.opBoolean","SPLIT",FACE,{"disambiguationData":[TD([makeQuery(id+"F3.opExtrude","SWEPT_FACE",FACE,{"disambiguationData":[OSD([subQ29])]})])],"derivedFrom":makeQuery(id+"F7.opExtrude","CAP_FACE",FACE,{"disambiguationData":[OSD([sQuery(id+"F6.wireOp",EDGE,"E5.bottom"),subQ33,subQ34,sQuery(id+"F6.wireOp",EDGE,"E5.right"),subQ26,subQ25,subQ24,subQ23,subQ22,subQ27,subQ35,subQ36,subQ37,subQ38,subQ39,subQ30,subQ40,subQ32,subQ41,subQ42,subQ43,subQ44,subQ21,subQ20,subQ19,subQ18,subQ17,subQ16,subQ15,subQ14,subQ13,subQ12,subQ11,subQ10,subQ9,subQ8,subQ7,subQ6,subQ28,subQ5,subQ31,subQ4,subQ3,subQ2,subQ1,subQ0,subQ45,subQ46,subQ47,subQ48,subQ49,sQuery(id+"F6.wireOp",EDGE,"E7.47.0.0"),sQuery(id+"F6.wireOp",EDGE,"E7.48.0.0"),sQuery(id+"F6.wireOp",EDGE,"E7.49.0.0"),sQuery(id+"F6.wireOp",EDGE,"E7.50.0.0"),sQuery(id+"F6.wireOp",EDGE,"E7.51.0.0"),sQuery(id+"F6.wireOp",EDGE,"E7.52.0.0"),sQuery(id+"F6.wireOp",EDGE,"E7.53.0.0")])],"isStart":true})});}
            var sketch = newSketch(context, id + "F17", { "sketchPlane" : qUnion([Q0])});
            skLineSegment(sketch, "E20.bottom", {"start": v(-190.5, -502.92) * mm, "end": v(196.85, -502.92) * mm});
            skLineSegment(sketch, "E20.top", {"start": v(-190.5, -248.92) * mm, "end": v(196.85, -248.92) * mm});
            skLineSegment(sketch, "E20.left", {"start": v(-190.5, -502.92) * mm, "end": v(-190.5, -248.92) * mm});
            skLineSegment(sketch, "E20.right", {"start": v(196.85, -502.92) * mm, "end": v(196.85, -248.92) * mm});
            skSolve(sketch);
        }
        {
            var Q0;
            Q0=qSketchRegion(id+"F17",true);
            extrude(context, id + "F18", {"entities" : qUnion([Q0]), "depth" : 12.7 * mm, "offsetDistance" : 25.4 * mm});
        }
        {
            var Q0;
            Q0=makeQuery(id+"F5.opExtrude","CAP_FACE",FACE,{"disambiguationData":[OSD([sQuery(id+"F4.wireOp",EDGE,"E2.bottom"),sQuery(id+"F4.wireOp",EDGE,"E2.top"),sQuery(id+"F4.wireOp",EDGE,"E2.left"),sQuery(id+"F4.wireOp",EDGE,"E2.right"),sQuery(id+"F4.wireOp",EDGE,"E3"),sQuery(id+"F4.wireOp",EDGE,"E4.0.1.0"),sQuery(id+"F4.wireOp",EDGE,"E4.1.0.0"),sQuery(id+"F4.wireOp",EDGE,"E4.1.1.0"),sQuery(id+"F4.wireOp",EDGE,"E4.2.0.0"),sQuery(id+"F4.wireOp",EDGE,"E4.2.1.0"),sQuery(id+"F4.wireOp",EDGE,"E4.3.0.0"),sQuery(id+"F4.wireOp",EDGE,"E4.3.1.0"),sQuery(id+"F4.wireOp",EDGE,"E4.4.0.0"),sQuery(id+"F4.wireOp",EDGE,"E4.4.1.0"),sQuery(id+"F4.wireOp",EDGE,"E4.5.0.0"),sQuery(id+"F4.wireOp",EDGE,"E4.5.1.0"),sQuery(id+"F4.wireOp",EDGE,"E4.6.0.0"),sQuery(id+"F4.wireOp",EDGE,"E4.6.1.0"),sQuery(id+"F4.wireOp",EDGE,"E4.7.0.0"),sQuery(id+"F4.wireOp",EDGE,"E4.7.1.0"),sQuery(id+"F4.wireOp",EDGE,"E4.8.0.0"),sQuery(id+"F4.wireOp",EDGE,"E4.8.1.0"),sQuery(id+"F4.wireOp",EDGE,"E4.9.0.0"),sQuery(id+"F4.wireOp",EDGE,"E4.9.1.0"),sQuery(id+"F4.wireOp",EDGE,"E4.10.0.0"),sQuery(id+"F4.wireOp",EDGE,"E4.10.1.0"),sQuery(id+"F4.wireOp",EDGE,"E4.11.0.0"),sQuery(id+"F4.wireOp",EDGE,"E4.11.1.0"),sQuery(id+"F4.wireOp",EDGE,"E4.12.0.0"),sQuery(id+"F4.wireOp",EDGE,"E4.12.1.0"),sQuery(id+"F4.wireOp",EDGE,"E4.13.0.0"),sQuery(id+"F4.wireOp",EDGE,"E4.13.1.0"),sQuery(id+"F4.wireOp",EDGE,"E4.14.0.0"),sQuery(id+"F4.wireOp",EDGE,"E4.14.1.0"),sQuery(id+"F4.wireOp",EDGE,"E4.15.0.0"),sQuery(id+"F4.wireOp",EDGE,"E4.15.1.0"),sQuery(id+"F4.wireOp",EDGE,"E4.16.0.0"),sQuery(id+"F4.wireOp",EDGE,"E4.16.1.0"),sQuery(id+"F4.wireOp",EDGE,"E4.17.0.0"),sQuery(id+"F4.wireOp",EDGE,"E4.17.1.0"),sQuery(id+"F4.wireOp",EDGE,"E4.18.0.0"),sQuery(id+"F4.wireOp",EDGE,"E4.18.1.0"),sQuery(id+"F4.wireOp",EDGE,"E4.19.0.0"),sQuery(id+"F4.wireOp",EDGE,"E4.19.1.0"),sQuery(id+"F4.wireOp",EDGE,"E4.20.0.0"),sQuery(id+"F4.wireOp",EDGE,"E4.20.1.0"),sQuery(id+"F4.wireOp",EDGE,"E4.21.0.0"),sQuery(id+"F4.wireOp",EDGE,"E4.21.1.0"),sQuery(id+"F4.wireOp",EDGE,"E4.22.0.0"),sQuery(id+"F4.wireOp",EDGE,"E4.22.1.0"),sQuery(id+"F4.wireOp",EDGE,"E4.23.0.0"),sQuery(id+"F4.wireOp",EDGE,"E4.23.1.0"),sQuery(id+"F4.wireOp",EDGE,"E4.24.0.0"),sQuery(id+"F4.wireOp",EDGE,"E4.24.1.0"),sQuery(id+"F4.wireOp",EDGE,"E4.25.0.0"),sQuery(id+"F4.wireOp",EDGE,"E4.25.1.0"),sQuery(id+"F4.wireOp",EDGE,"E4.26.0.0"),sQuery(id+"F4.wireOp",EDGE,"E4.26.1.0"),sQuery(id+"F4.wireOp",EDGE,"E4.27.0.0"),sQuery(id+"F4.wireOp",EDGE,"E4.27.1.0"),sQuery(id+"F4.wireOp",EDGE,"E4.28.0.0"),sQuery(id+"F4.wireOp",EDGE,"E4.28.1.0"),sQuery(id+"F4.wireOp",EDGE,"E4.29.0.0"),sQuery(id+"F4.wireOp",EDGE,"E4.29.1.0"),sQuery(id+"F4.wireOp",EDGE,"E4.30.0.0"),sQuery(id+"F4.wireOp",EDGE,"E4.30.1.0"),sQuery(id+"F4.wireOp",EDGE,"E4.31.0.0"),sQuery(id+"F4.wireOp",EDGE,"E4.31.1.0"),sQuery(id+"F4.wireOp",EDGE,"E4.32.0.0"),sQuery(id+"F4.wireOp",EDGE,"E4.32.1.0"),sQuery(id+"F4.wireOp",EDGE,"E4.33.0.0"),sQuery(id+"F4.wireOp",EDGE,"E4.33.1.0"),sQuery(id+"F4.wireOp",EDGE,"E4.34.0.0"),sQuery(id+"F4.wireOp",EDGE,"E4.34.1.0"),sQuery(id+"F4.wireOp",EDGE,"E4.35.0.0"),sQuery(id+"F4.wireOp",EDGE,"E4.35.1.0"),sQuery(id+"F4.wireOp",EDGE,"E4.36.0.0"),sQuery(id+"F4.wireOp",EDGE,"E4.36.1.0"),sQuery(id+"F4.wireOp",EDGE,"E4.37.0.0"),sQuery(id+"F4.wireOp",EDGE,"E4.37.1.0"),sQuery(id+"F4.wireOp",EDGE,"E4.38.0.0"),sQuery(id+"F4.wireOp",EDGE,"E4.38.1.0"),sQuery(id+"F4.wireOp",EDGE,"E4.39.0.0"),sQuery(id+"F4.wireOp",EDGE,"E4.39.1.0"),sQuery(id+"F4.wireOp",EDGE,"E4.40.0.0"),sQuery(id+"F4.wireOp",EDGE,"E4.40.1.0"),sQuery(id+"F4.wireOp",EDGE,"E4.41.0.0"),sQuery(id+"F4.wireOp",EDGE,"E4.41.1.0"),sQuery(id+"F4.wireOp",EDGE,"E4.42.0.0"),sQuery(id+"F4.wireOp",EDGE,"E4.42.1.0"),sQuery(id+"F4.wireOp",EDGE,"E4.43.0.0"),sQuery(id+"F4.wireOp",EDGE,"E4.43.1.0"),sQuery(id+"F4.wireOp",EDGE,"E4.44.0.0"),sQuery(id+"F4.wireOp",EDGE,"E4.44.1.0"),sQuery(id+"F4.wireOp",EDGE,"E4.45.0.0"),sQuery(id+"F4.wireOp",EDGE,"E4.45.1.0"),sQuery(id+"F4.wireOp",EDGE,"E4.46.0.0"),sQuery(id+"F4.wireOp",EDGE,"E4.46.1.0"),sQuery(id+"F4.wireOp",EDGE,"E4.47.0.0"),sQuery(id+"F4.wireOp",EDGE,"E4.47.1.0"),sQuery(id+"F4.wireOp",EDGE,"E4.48.0.0"),sQuery(id+"F4.wireOp",EDGE,"E4.48.1.0"),sQuery(id+"F4.wireOp",EDGE,"E4.49.0.0"),sQuery(id+"F4.wireOp",EDGE,"E4.49.1.0"),sQuery(id+"F4.wireOp",EDGE,"E4.50.0.0"),sQuery(id+"F4.wireOp",EDGE,"E4.50.1.0"),sQuery(id+"F4.wireOp",EDGE,"E4.51.0.0"),sQuery(id+"F4.wireOp",EDGE,"E4.51.1.0"),sQuery(id+"F4.wireOp",EDGE,"E4.52.0.0"),sQuery(id+"F4.wireOp",EDGE,"E4.52.1.0"),sQuery(id+"F4.wireOp",EDGE,"E4.53.0.0"),sQuery(id+"F4.wireOp",EDGE,"E4.53.1.0")])],"isStart":true});
            var sketch = newSketch(context, id + "F19", { "sketchPlane" : qUnion([Q0])});
            skLineSegment(sketch, "E21.bottom", {"start": v(-146.05, -469.9) * mm, "end": v(146.05, -469.9) * mm});
            skLineSegment(sketch, "E21.top", {"start": v(-146.05, -508) * mm, "end": v(146.05, -508) * mm});
            skLineSegment(sketch, "E21.left", {"start": v(-146.05, -469.9) * mm, "end": v(-146.05, -508) * mm});
            skLineSegment(sketch, "E21.right", {"start": v(146.05, -469.9) * mm, "end": v(146.05, -508) * mm});
            skSolve(sketch);
        }
        {
            var Q0;
            Q0 = qSketchRegion(id + "F19", true);
            extrude(context, id + "F20", {"entities" : qUnion([Q0]), "operationType" : NewBodyOperationType.REMOVE, "endBound" : BoundingType.THROUGH_ALL, "oppositeDirection" : true, "depth" : 25.4 * mm, "offsetDistance" : 25.4 * mm});
        }
        {
            var Q0;
            Q0=makeQuery(id+"F18.opExtrude","CAP_FACE",FACE,{"disambiguationData":[OSD([sQuery(id+"F17.wireOp",EDGE,"E20.bottom"),sQuery(id+"F17.wireOp",EDGE,"E20.top"),sQuery(id+"F17.wireOp",EDGE,"E20.left"),sQuery(id+"F17.wireOp",EDGE,"E20.right")])],"isStart":false});
            var sketch = newSketch(context, id + "F21", { "sketchPlane" : qUnion([Q0])});
            skLineSegment(sketch, "E22.bottom", {"start": v(196.85, -502.92) * mm, "end": v(-190.5, -502.92) * mm});
            skLineSegment(sketch, "E22.top", {"start": v(196.85, -325.12) * mm, "end": v(-190.5, -325.12) * mm});
            skLineSegment(sketch, "E22.left", {"start": v(196.85, -502.92) * mm, "end": v(196.85, -325.12) * mm});
            skLineSegment(sketch, "E22.right", {"start": v(-190.5, -502.92) * mm, "end": v(-190.5, -325.12) * mm});
            skSolve(sketch);
        }
        {
            var Q0;
            {var subQ1=makeQuery(id+"F18.opExtrude","CAP_FACE",FACE,{"disambiguationData":[OSD([sQuery(id+"F17.wireOp",EDGE,"E20.bottom"),sQuery(id+"F17.wireOp",EDGE,"E20.top"),sQuery(id+"F17.wireOp",EDGE,"E20.left"),sQuery(id+"F17.wireOp",EDGE,"E20.right")])],"isStart":false});Q0=makeQuery(id+"F21.imprint","IMPRINT",FACE,{"disambiguationData":[TD([[makeQuery(id+"F21.imprint","IMPRINT",EDGE,{"derivedFrom":makeQuery(id+"F20.boolean.opBoolean","INTERSECT",EDGE,{"derivedFrom":[subQ1,makeQuery(id+"F20.opExtrude","SWEPT_FACE",FACE,{"disambiguationData":[OSD([sQuery(id+"F19.wireOp",EDGE,"E21.bottom")])]})]})}),-1.0]])]});}
            var Q1;
            Q1=makeQuery(id+"F21.imprint","IMPRINT",FACE,{"disambiguationData":[TD([[makeQuery(id+"F21.imprint","IMPRINT",EDGE,{"derivedFrom":sQuery(id+"F21.wireOp",EDGE,"E22.top")}),1.0]])]});
            extrude(context, id + "F22", {"entities" : qUnion([Q0, Q1]), "operationType" : NewBodyOperationType.REMOVE, "endBound" : BoundingType.UP_TO_NEXT, "oppositeDirection" : true, "depth" : 12.7 * mm, "offsetDistance" : 25.4 * mm});
        }
        {
            var Q0;
            {var subQ6=sQuery(id+"F2.wireOp",EDGE,"E1.right");var subQ8=sQuery(id+"F2.wireOp",EDGE,"E1.bottom");var subQ38=sQuery(id+"F2.wireOp",EDGE,"E1.left");var subQ39=makeQuery(id+"F3.opExtrude","CAP_FACE",FACE,{"disambiguationData":[OSD([subQ8,sQuery(id+"F2.wireOp",EDGE,"E1.top"),subQ38,subQ6])],"isStart":false});Q0=makeQuery(id+"F20.boolean.opBoolean","SPLIT",FACE,{"disambiguationData":[TD([makeQuery(id+"F14.opPattern","COPY",FACE,{"derivedFrom":makeQuery(id+"F9.opExtrude","SWEPT_FACE",FACE,{"disambiguationData":[OSD([sQuery(id+"F8.wireOp",EDGE,"E8.top")])]}),"instanceName":"1"})])],"derivedFrom":makeQuery(id+"F14.opPattern","COPY",FACE,{"derivedFrom":subQ39,"instanceName":"1"})});}
            var sketch = newSketch(context, id + "F23", { "sketchPlane" : qUnion([Q0])});
            skLineSegment(sketch, "E23.bottom", {"start": v(196.85, 106.68) * mm, "end": v(146.05, 106.68) * mm});
            skLineSegment(sketch, "E23.top", {"start": v(196.85, 81.28) * mm, "end": v(146.05, 81.28) * mm});
            skLineSegment(sketch, "E23.left", {"start": v(196.85, 106.68) * mm, "end": v(196.85, 81.28) * mm});
            skLineSegment(sketch, "E23.right", {"start": v(146.05, 106.68) * mm, "end": v(146.05, 81.28) * mm});
            skLineSegment(sketch, "E24.MirrorCS", {"start": v(-196.85, 106.68) * mm, "end": v(-146.05, 106.68) * mm});
            skLineSegment(sketch, "E25.MirrorCS", {"start": v(-146.05, 106.68) * mm, "end": v(-146.05, 81.28) * mm});
            skLineSegment(sketch, "E26.MirrorCS", {"start": v(-196.85, 106.68) * mm, "end": v(-196.85, 81.28) * mm});
            skLineSegment(sketch, "E27.MirrorCS", {"start": v(-196.85, 81.28) * mm, "end": v(-146.05, 81.28) * mm});
            skSolve(sketch);
        }
        {
            var Q0;
            Q0 = qSketchRegion(id + "F23", true);
            extrude(context, id + "F24", {"entities" : qUnion([Q0]), "depth" : 177.8 * mm, "offsetDistance" : 25.4 * mm});
        }
        {
            var Q0;
            Q0=makeQuery(id+"F24.opExtrude","CAP_FACE",FACE,{"disambiguationData":[OSD([sQuery(id+"F23.wireOp",EDGE,"E23.bottom"),sQuery(id+"F23.wireOp",EDGE,"E23.top"),sQuery(id+"F23.wireOp",EDGE,"E23.left"),sQuery(id+"F23.wireOp",EDGE,"E23.right")])],"isStart":false});
            var sketch = newSketch(context, id + "F25", { "sketchPlane" : qUnion([Q0])});
            skLineSegment(sketch, "E28.bottom", {"start": v(-260.35, 106.68) * mm, "end": v(260.35, 106.68) * mm});
            skLineSegment(sketch, "E28.top", {"start": v(-260.35, 81.28) * mm, "end": v(260.35, 81.28) * mm});
            skLineSegment(sketch, "E28.left", {"start": v(-260.35, 106.68) * mm, "end": v(-260.35, 81.28) * mm});
            skLineSegment(sketch, "E28.right", {"start": v(260.35, 106.68) * mm, "end": v(260.35, 81.28) * mm});
            skSolve(sketch);
        }
        {
            var Q0;
            Q0 = qSketchRegion(id + "F25", true);
            extrude(context, id + "F26", {"entities" : qUnion([Q0]), "depth" : 25.4 * mm, "offsetDistance" : 25.4 * mm});
        }
        {
            var Q0;
            Q0=makeQuery(id+"F24.opExtrude","SWEPT_FACE",FACE,{"disambiguationData":[OSD([sQuery(id+"F23.wireOp",EDGE,"E23.right")])]});
            var sketch = newSketch(context, id + "F27", { "sketchPlane" : qUnion([Q0])});
            skLineSegment(sketch, "E29.bottom", {"start": v(-426.72, 93.98) * mm, "end": v(-388.62, 93.98) * mm});
            skLineSegment(sketch, "E29.top", {"start": v(-426.72, 119.38) * mm, "end": v(-388.62, 119.38) * mm});
            skLineSegment(sketch, "E29.left", {"start": v(-426.72, 93.98) * mm, "end": v(-426.72, 119.38) * mm});
            skLineSegment(sketch, "E29.right", {"start": v(-388.62, 93.98) * mm, "end": v(-388.62, 119.38) * mm});
            skLineSegment(sketch, "E30", {"start": v(-426.72, 119.38) * mm, "end": v(-415.86, 144.78) * mm});
            skLineSegment(sketch, "E31", {"start": v(-415.86, 144.78) * mm, "end": v(-399.48, 144.78) * mm});
            skLineSegment(sketch, "E32", {"start": v(-399.48, 144.78) * mm, "end": v(-388.62, 119.38) * mm});
            skCircle(sketch, "E33", {"center": v(-407.67, 130.45) * mm, "radius": 6.35 * mm});
            skPoint(sketch, "E33.centerSnap0", {"position": v(-407.67, 144.78) * mm});
            skSolve(sketch);
        }
        {
            var Q0;
            Q0 = qSketchRegion(id + "F27", true);
            extrude(context, id + "F28", {"entities" : qUnion([Q0]), "operationType" : NewBodyOperationType.ADD, "depth" : 5.08 * mm, "offsetDistance" : 25.4 * mm});
        }
        {
            var Q0;
            Q0=makeQuery(id+"F24.opExtrude","SWEPT_BODY",BODY,{"disambiguationData":[OSD([sQuery(id+"F23.wireOp",EDGE,"E23.bottom"),sQuery(id+"F23.wireOp",EDGE,"E23.top"),sQuery(id+"F23.wireOp",EDGE,"E23.left"),sQuery(id+"F23.wireOp",EDGE,"E23.right")])]});
            var Q1;
            Q1=qCreatedBy(makeId("Right.planeOp"),FACE);
            mirror(context, id + "F29", {"entities" : qUnion([Q0]), "mirrorPlane" : qUnion([Q1])});
        }
    });
